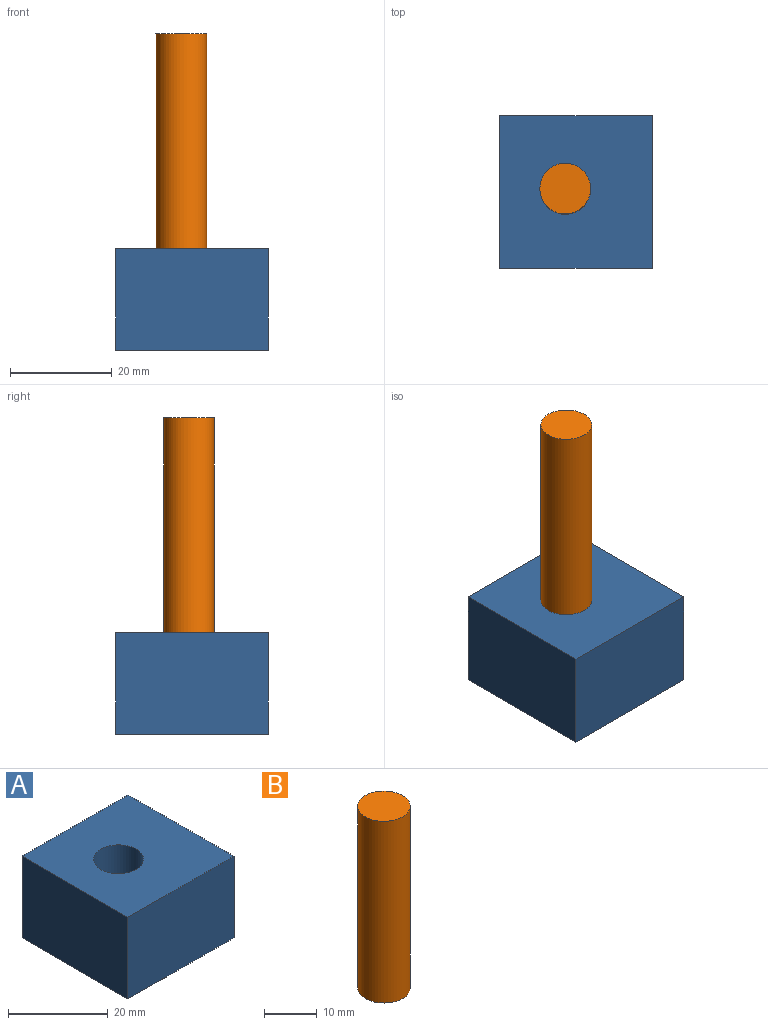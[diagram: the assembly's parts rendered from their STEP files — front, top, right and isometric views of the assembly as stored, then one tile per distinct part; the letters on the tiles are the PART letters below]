
ASSEMBLY  parts=2 mates=1
PART A: 7 faces, bbox 30x30x20 mm
  f0: plane 30x20mm, normal (0,1,0), area 600mm2, adj f1,f3,f4,f5
  f1: plane 30x20mm, normal (-1,0,0), area 600mm2, adj f0,f2,f4,f5
  f2: plane 30x20mm, normal (0,-1,0), area 600mm2, adj f1,f3,f4,f5
  f3: plane 30x20mm, normal (1,0,0), area 600mm2, adj f0,f2,f4,f5
  f4: plane 30x30mm, normal (0,0,1), area 821.5mm2, adj f0,f1,f2,f3,f6
  f5: plane 30x30mm, normal (0,0,-1), area 821.5mm2, adj f0,f1,f2,f3,f6
  f6: cylinder r=5mm len=20mm, axis (0,0,1), area 628.3mm2, adj f4,f5
PART B: 3 faces, bbox 10x10x42.3 mm
  f0: cylinder r=5mm len=42.3mm, axis (0,0,1), area 1328.9mm2, adj f1,f2
  f1: plane 10x10mm, normal (0,0,-1), area 78.5mm2, adj f0
  f2: plane 10x10mm, normal (0,0,1), area 78.5mm2, adj f0
PLACE A t=(-1.44,-15.13,8.46)mm
PLACE B t=(-41.44,-15.13,29.64)mm
MATE slider B.f0 <-> A.f6  axis (0,0,1) through (-33.08,0.45,39.59)mm
